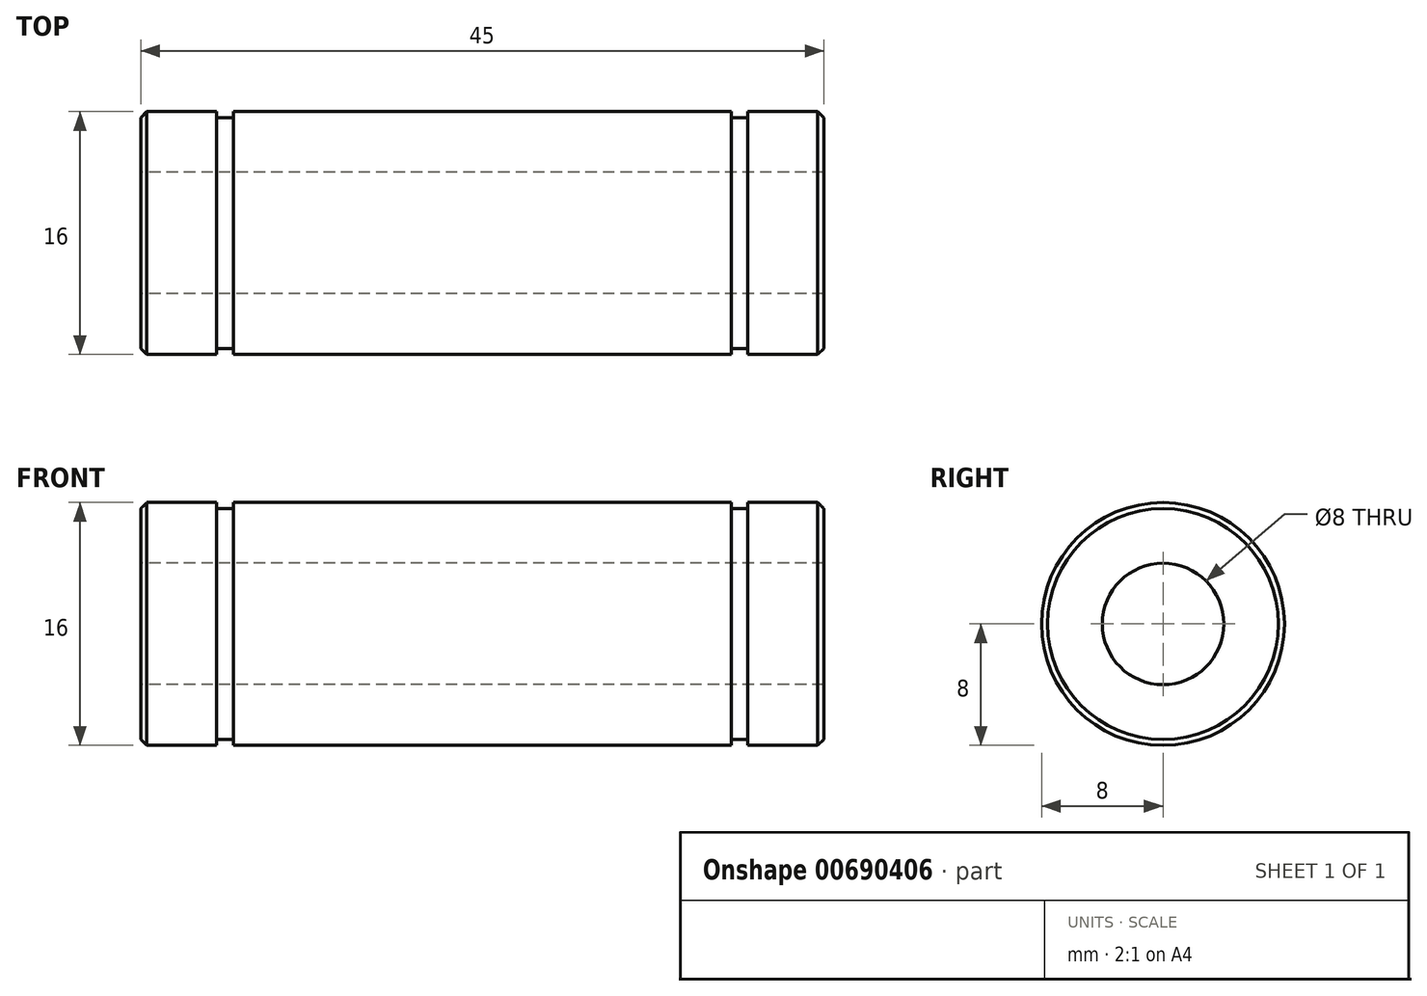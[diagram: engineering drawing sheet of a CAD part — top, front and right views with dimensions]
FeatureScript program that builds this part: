
annotation { "Feature Type Name" : "Feature", "Feature Type Description" : "" }
export const myFeature = defineFeature(function(context is Context, id is Id, definition is map)
    precondition{}
    {
        {
            var Q0;
            Q0=qCreatedBy(makeId("Front.planeOp"),FACE);
            var sketch = newSketch(context, id + "F0", { "sketchPlane" : qUnion([Q0])});
            skLineSegment(sketch, "E0", {"start": v(0, 0) * mm, "end": v(10.81, 0) * mm, "construction": true});
            skLineSegment(sketch, "E1", {"start": v(0, 0) * mm, "end": v(0, 8) * mm, "construction": true});
            skLineSegment(sketch, "E2", {"start": v(0, 8) * mm, "end": v(16.4, 8) * mm});
            skLineSegment(sketch, "E3", {"start": v(16.4, 8) * mm, "end": v(16.4, 7.6) * mm});
            skLineSegment(sketch, "E4", {"start": v(16.4, 7.6) * mm, "end": v(17.5, 7.6) * mm});
            skLineSegment(sketch, "E5", {"start": v(17.5, 7.6) * mm, "end": v(17.5, 8) * mm});
            skLineSegment(sketch, "E6", {"start": v(17.5, 8) * mm, "end": v(22.1, 8) * mm});
            skLineSegment(sketch, "E7", {"start": v(22.1, 8) * mm, "end": v(22.5, 7.6) * mm});
            skLineSegment(sketch, "E8", {"start": v(22.5, 7.6) * mm, "end": v(22.5, 4) * mm});
            skLineSegment(sketch, "E9", {"start": v(22.5, 4) * mm, "end": v(0, 4) * mm});
            skLineSegment(sketch, "E10.MirrorCS", {"start": v(0, 8) * mm, "end": v(-16.4, 8) * mm});
            skLineSegment(sketch, "E11.MirrorCS", {"start": v(-16.4, 8) * mm, "end": v(-16.4, 7.6) * mm});
            skLineSegment(sketch, "E12.MirrorCS", {"start": v(-16.4, 7.6) * mm, "end": v(-17.5, 7.6) * mm});
            skLineSegment(sketch, "E13.MirrorCS", {"start": v(-17.5, 7.6) * mm, "end": v(-17.5, 8) * mm});
            skLineSegment(sketch, "E14.MirrorCS", {"start": v(-17.5, 8) * mm, "end": v(-22.1, 8) * mm});
            skLineSegment(sketch, "E15.MirrorCS", {"start": v(-22.1, 8) * mm, "end": v(-22.5, 7.6) * mm});
            skLineSegment(sketch, "E16.MirrorCS", {"start": v(-22.5, 4) * mm, "end": v(0, 4) * mm});
            skLineSegment(sketch, "E17.MirrorCS", {"start": v(-22.5, 7.6) * mm, "end": v(-22.5, 4) * mm});
            skSolve(sketch);
        }
        {
            var Q0;
            Q0 = qSketchRegion(id + "F0", true);
            var Q1;
            Q1=sQuery(id+"F0.wireOp",EDGE,"E0");
            revolve(context, id + "F1", {"entities" : qUnion([Q0]), "axis" : qUnion([Q1]), "revolveType" : RevolveType.FULL});
        }
    });
